# Revit family: M-OBR4-GRD
name_source: partatom
category: Mechanical Equipment
revit_build: Autodesk Revit MEP 2016 (Build: 20150220_1215(x64)
units: mm (PartAtom-declared; Revit-internal decimal feet)

## family parameters
Cut with Voids When Loaded = No
Host = Face
OmniClass Number = 23.65.70.14.11
OmniClass Title = Drinking Fountains/Coolers
Part Type = Normal
Room Calculation Point = No
Round Connector Dimension = Use Diameter
Shared = Yes

## types (1)
- M-OBR4-GRD
    Amperage = 0
    CW Connection = Yes
    Default Elevation = 29 "
    Description = Recessed Outdoor Bottle Filler With Bi-Level Drinking Fountain
    HW Connection = No
    M-OBR4-GRD- Recessed Outdoor Bottle Filler With Bi-Level Drinking Fountain = Yes
    Manufacturer = Murdock
    Material = Stainless Steel
    Model = M-OBR4-GRD
    OVERALL DEPTH = 4
    OVERALL SIZE HEIGHT = 32.625
    OVERALL SIZE WIDTH = 36.5
    Revised Date = 05/18/18
    Tempered Water Connection = No
    URL = https://www.murdockmfg.com
    Vent Connection = No
    Voltage = 0
    Waste Connection = Yes

## geometry (parser evidence)
native form markers: Sweep x8
no freeform markers — native parametric forms only
